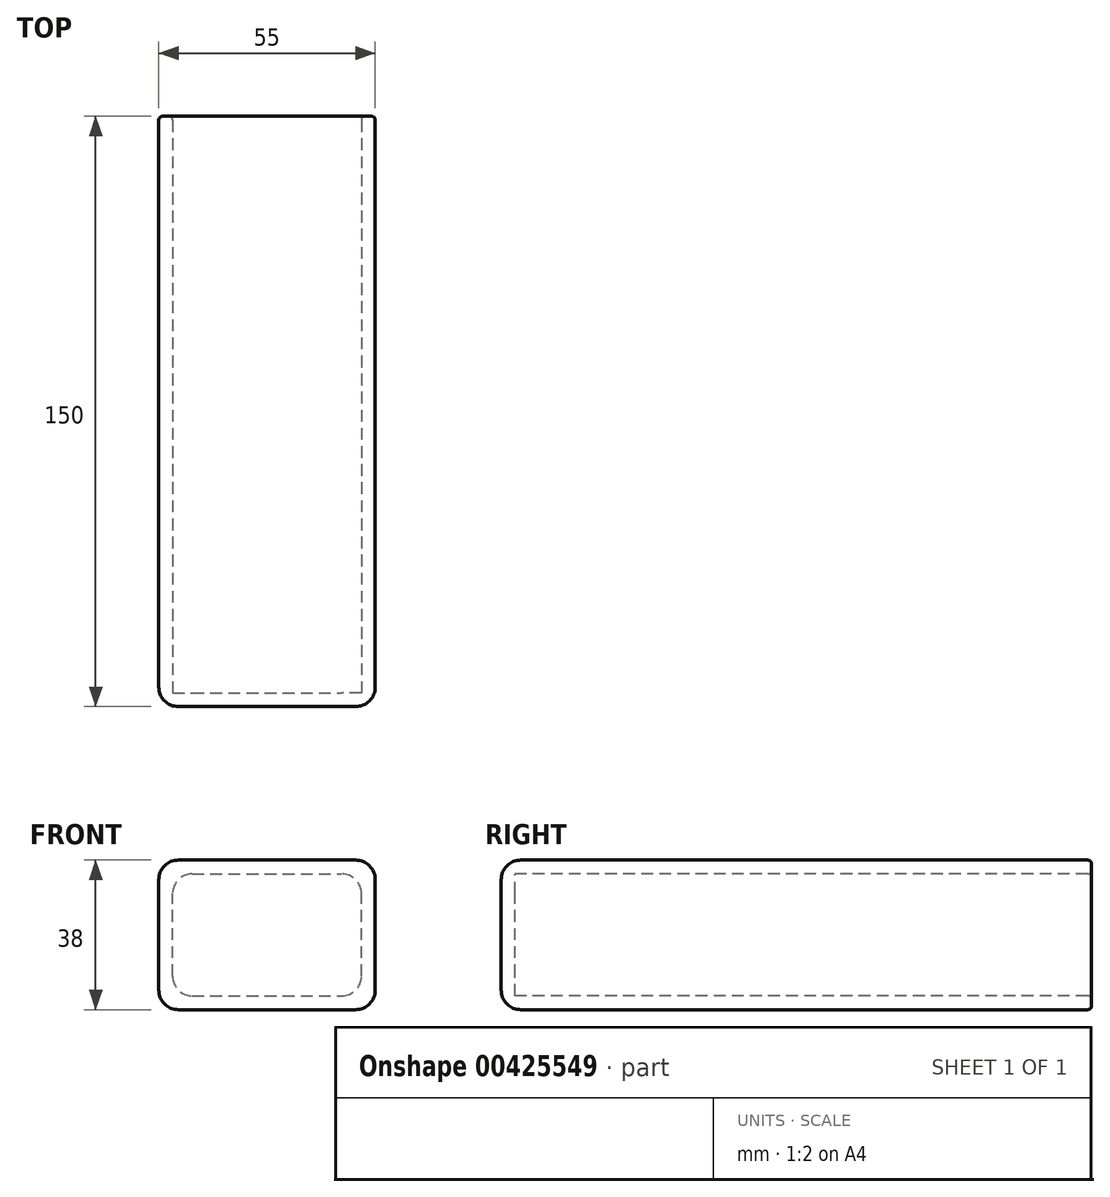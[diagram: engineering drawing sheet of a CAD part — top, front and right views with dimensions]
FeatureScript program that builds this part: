
annotation { "Feature Type Name" : "Feature", "Feature Type Description" : "" }
export const myFeature = defineFeature(function(context is Context, id is Id, definition is map)
    precondition{}
    {
        {
            var Q0;
            Q0=qCreatedBy(makeId("Front.planeOp"),FACE);
            var sketch = newSketch(context, id + "F0", { "sketchPlane" : qUnion([Q0])});
            skLineSegment(sketch, "E0.bottom", {"start": v(5, 0) * mm, "end": v(50, 0) * mm});
            skLineSegment(sketch, "E0.top", {"start": v(5, 38) * mm, "end": v(50, 38) * mm});
            skLineSegment(sketch, "E0.left", {"start": v(0, 5) * mm, "end": v(0, 33) * mm});
            skLineSegment(sketch, "E0.right", {"start": v(55, 5) * mm, "end": v(55, 33) * mm});
            skLineSegment(sketch, "E1.bottom", {"start": v(8.5, 3.5) * mm, "end": v(46.5, 3.5) * mm});
            skLineSegment(sketch, "E1.top", {"start": v(8.5, 34.5) * mm, "end": v(46.5, 34.5) * mm});
            skLineSegment(sketch, "E1.left", {"start": v(3.5, 8.5) * mm, "end": v(3.5, 29.5) * mm});
            skLineSegment(sketch, "E1.right", {"start": v(51.5, 8.5) * mm, "end": v(51.5, 29.5) * mm});
            skPoint(sketch, "E2.visualSharp", {"position": v(51.5, 34.5) * mm});
            skArc(sketch, "E2.filletArc", {"start": v(51.5, 29.5) * mm, "mid": v(50.04, 33.04) * mm, "end": v(46.5, 34.5) * mm});
            skPoint(sketch, "E3.visualSharp", {"position": v(55, 38) * mm});
            skArc(sketch, "E3.filletArc", {"start": v(55, 33) * mm, "mid": v(53.54, 36.54) * mm, "end": v(50, 38) * mm});
            skPoint(sketch, "E4.visualSharp", {"position": v(3.5, 34.5) * mm});
            skArc(sketch, "E4.filletArc", {"start": v(8.5, 34.5) * mm, "mid": v(4.96, 33.04) * mm, "end": v(3.5, 29.5) * mm});
            skPoint(sketch, "E5.visualSharp", {"position": v(0, 38) * mm});
            skArc(sketch, "E5.filletArc", {"start": v(5, 38) * mm, "mid": v(1.46, 36.54) * mm, "end": v(0, 33) * mm});
            skPoint(sketch, "E6.visualSharp", {"position": v(51.5, 3.5) * mm});
            skArc(sketch, "E6.filletArc", {"start": v(46.5, 3.5) * mm, "mid": v(50.04, 4.96) * mm, "end": v(51.5, 8.5) * mm});
            skPoint(sketch, "E7.visualSharp", {"position": v(3.5, 3.5) * mm});
            skArc(sketch, "E7.filletArc", {"start": v(3.5, 8.5) * mm, "mid": v(4.96, 4.96) * mm, "end": v(8.5, 3.5) * mm});
            skPoint(sketch, "E8.visualSharp", {"position": v(55, 0) * mm});
            skArc(sketch, "E8.filletArc", {"start": v(50, 0) * mm, "mid": v(53.54, 1.46) * mm, "end": v(55, 5) * mm});
            skPoint(sketch, "E9.visualSharp", {"position": v(0, 0) * mm});
            skArc(sketch, "E9.filletArc", {"start": v(0, 5) * mm, "mid": v(1.46, 1.46) * mm, "end": v(5, 0) * mm});
            skSolve(sketch);
        }
        {
            var Q0;
            Q0=makeQuery(id+"F0.imprint","IMPRINT",FACE,{"disambiguationData":[TD([[makeQuery(id+"F0.imprint","IMPRINT",EDGE,{"derivedFrom":sQuery(id+"F0.wireOp",EDGE,"E1.bottom")}),1.0]])]});
            extrude(context, id + "F1", {"entities" : qUnion([Q0]), "oppositeDirection" : true, "depth" : 3.5 * mm});
        }
        {
            var Q0;
            Q0=makeQuery(id+"F0.imprint","IMPRINT",FACE,{"disambiguationData":[TD([[makeQuery(id+"F0.imprint","IMPRINT",EDGE,{"derivedFrom":sQuery(id+"F0.wireOp",EDGE,"E0.bottom")}),1.0]])]});
            extrude(context, id + "F2", {"entities" : qUnion([Q0]), "operationType" : NewBodyOperationType.ADD, "oppositeDirection" : true, "depth" : 150 * mm});
        }
        {
            var Q0;
            Q0=makeQuery(id+"F2.opExtrude","CAP_EDGE",EDGE,{"disambiguationData":[OSD([sQuery(id+"F0.wireOp",EDGE,"E5.filletArc")])],"isStart":true});
            var Q1;
            Q1=makeQuery(id+"F2.opExtrude","CAP_EDGE",EDGE,{"disambiguationData":[OSD([sQuery(id+"F0.wireOp",EDGE,"E0.left")])],"isStart":true});
            var Q2;
            Q2=makeQuery(id+"F2.opExtrude","CAP_EDGE",EDGE,{"disambiguationData":[OSD([sQuery(id+"F0.wireOp",EDGE,"E0.top")])],"isStart":true});
            var Q3;
            Q3=makeQuery(id+"F2.opExtrude","CAP_EDGE",EDGE,{"disambiguationData":[OSD([sQuery(id+"F0.wireOp",EDGE,"E3.filletArc")])],"isStart":true});
            var Q4;
            Q4=makeQuery(id+"F2.opExtrude","CAP_EDGE",EDGE,{"disambiguationData":[OSD([sQuery(id+"F0.wireOp",EDGE,"E0.right")])],"isStart":true});
            var Q5;
            Q5=makeQuery(id+"F2.opExtrude","CAP_EDGE",EDGE,{"disambiguationData":[OSD([sQuery(id+"F0.wireOp",EDGE,"E8.filletArc")])],"isStart":true});
            var Q6;
            Q6=makeQuery(id+"F2.opExtrude","CAP_EDGE",EDGE,{"disambiguationData":[OSD([sQuery(id+"F0.wireOp",EDGE,"E0.bottom")])],"isStart":true});
            var Q7;
            Q7=makeQuery(id+"F2.opExtrude","CAP_EDGE",EDGE,{"disambiguationData":[OSD([sQuery(id+"F0.wireOp",EDGE,"E9.filletArc")])],"isStart":true});
            fillet(context, id + "F3", {"entities" : qUnion([Q0, Q1, Q2, Q3, Q4, Q5, Q6, Q7]), "radius" : 5 * mm, "tangentPropagation" : true, "allowEdgeOverflow" : false});
        }
        {
            var Q0;
            Q0=makeQuery(id+"F2.opExtrude","CAP_EDGE",EDGE,{"disambiguationData":[OSD([sQuery(id+"F0.wireOp",EDGE,"E0.top")])],"isStart":false});
            var Q1;
            Q1=makeQuery(id+"F2.opExtrude","CAP_EDGE",EDGE,{"disambiguationData":[OSD([sQuery(id+"F0.wireOp",EDGE,"E3.filletArc")])],"isStart":false});
            var Q2;
            Q2=makeQuery(id+"F2.opExtrude","CAP_EDGE",EDGE,{"disambiguationData":[OSD([sQuery(id+"F0.wireOp",EDGE,"E0.right")])],"isStart":false});
            var Q3;
            Q3=makeQuery(id+"F2.opExtrude","CAP_EDGE",EDGE,{"disambiguationData":[OSD([sQuery(id+"F0.wireOp",EDGE,"E8.filletArc")])],"isStart":false});
            var Q4;
            Q4=makeQuery(id+"F2.opExtrude","CAP_EDGE",EDGE,{"disambiguationData":[OSD([sQuery(id+"F0.wireOp",EDGE,"E0.bottom")])],"isStart":false});
            var Q5;
            Q5=makeQuery(id+"F2.opExtrude","CAP_EDGE",EDGE,{"disambiguationData":[OSD([sQuery(id+"F0.wireOp",EDGE,"E9.filletArc")])],"isStart":false});
            var Q6;
            Q6=makeQuery(id+"F2.opExtrude","CAP_EDGE",EDGE,{"disambiguationData":[OSD([sQuery(id+"F0.wireOp",EDGE,"E0.left")])],"isStart":false});
            var Q7;
            Q7=makeQuery(id+"F2.opExtrude","CAP_EDGE",EDGE,{"disambiguationData":[OSD([sQuery(id+"F0.wireOp",EDGE,"E5.filletArc")])],"isStart":false});
            var Q8;
            Q8=makeQuery(id+"F2.opExtrude","CAP_EDGE",EDGE,{"disambiguationData":[OSD([sQuery(id+"F0.wireOp",EDGE,"E1.left")])],"isStart":false});
            var Q9;
            Q9=makeQuery(id+"F2.opExtrude","CAP_EDGE",EDGE,{"disambiguationData":[OSD([sQuery(id+"F0.wireOp",EDGE,"E4.filletArc")])],"isStart":false});
            var Q10;
            Q10=makeQuery(id+"F2.opExtrude","CAP_EDGE",EDGE,{"disambiguationData":[OSD([sQuery(id+"F0.wireOp",EDGE,"E1.top")])],"isStart":false});
            var Q11;
            Q11=makeQuery(id+"F2.opExtrude","CAP_EDGE",EDGE,{"disambiguationData":[OSD([sQuery(id+"F0.wireOp",EDGE,"E2.filletArc")])],"isStart":false});
            var Q12;
            Q12=makeQuery(id+"F2.opExtrude","CAP_EDGE",EDGE,{"disambiguationData":[OSD([sQuery(id+"F0.wireOp",EDGE,"E1.right")])],"isStart":false});
            var Q13;
            Q13=makeQuery(id+"F2.opExtrude","CAP_EDGE",EDGE,{"disambiguationData":[OSD([sQuery(id+"F0.wireOp",EDGE,"E6.filletArc")])],"isStart":false});
            var Q14;
            Q14=makeQuery(id+"F2.opExtrude","CAP_EDGE",EDGE,{"disambiguationData":[OSD([sQuery(id+"F0.wireOp",EDGE,"E1.bottom")])],"isStart":false});
            var Q15;
            Q15=makeQuery(id+"F2.opExtrude","CAP_EDGE",EDGE,{"disambiguationData":[OSD([sQuery(id+"F0.wireOp",EDGE,"E7.filletArc")])],"isStart":false});
            fillet(context, id + "F4", {"entities" : qUnion([Q0, Q1, Q2, Q3, Q4, Q5, Q6, Q7, Q8, Q9, Q10, Q11, Q12, Q13, Q14, Q15]), "radius" : 1 * mm, "allowEdgeOverflow" : false});
        }
    });
